# Revit family: Hager-Vector-IP65-vacío-ES-es
name_source: partatom
category: Electrical Equipment
units: mm (PartAtom-declared; Revit-internal decimal feet)

## family parameters
Cut with Voids When Loaded = No
Host = Face
Panel Configuration = Two Columns, Circuits Across
Part Type = Panelboard
Room Calculation Point = No
Round Connector Dimension = Use Diameter
Shared = No

## types (4) — shared parameters
EF000003 - Tipo de montaje = EV000384 - Montado superficial (escayola)
EF000007 - Color = EV000270 - Gris
EF000116 - Número RAL = 7035
EF000339 - Tipo de cubierta = EV004216 - Puerta
EF001062 - Versión de EMC = Yes
EF001088 - Posibilidad de extensión = Yes
EF001134 - Carril DIN = No
EF001596 - Material de la carcasa = EV000139 - Plástico
EF004462 - Tipo de cierre = EV000154 - Otros
EF005474 - Grado de protección (IP) = EV006421 - IP65
EF006244 - Tapa/puerta transparente = No
EF006306 - Con cierre = Yes
EF009212 - Versión de la cubierta = EV000116 - Cerrado
EF015776 - Borne de tierra = No
EF015777 - Borne neutro = No
EF015941 - Puerta de transmisión de señal = No
HG000002 - Con puerta o tapa = Yes
HG000003 - Gama = Vector
HG000005 - Grosor = 3 mm  [stored 0.00984252 ft]
HG000006 - Empotrado = No
HG000009 - Puerta batiente doble = No
HG000010 - Puertas asimétricas = No
HG000011 - Filas vacías desde abajo = No
HG000017 - Distancia entre polos = 18 mm  [stored 0.0590551 ft]
Manufacturer = Hager
Type Comments = Vector
zero-valued in all types: Default Elevation, EF000266 - Número de filas, EF000332 - Altura de la instalación, EF000846 - Anchura de instalación, EF002950 - Anchura de unidades de división, HG000001 - Número de columnas, HG000007 - Número de columnas vacías, HG000008 - Número de filas vacías

## per-type parameters (varying)
| type | EF000008 - Anchura | EF000040 - Altura | EF000049 - Profundidad | EF000118 - Con placa de montaje | EF000218 - Profundidad de instalación | EF001131 - Profundidad interna | HG000004 - Referencia del fabricante | Model |
| Montado superficial IP65 A250 A350 P160 0 unidad de división - VP20G | 250 mm  [stored 0.82021 ft] | 350 mm | 160 mm | Yes | 160 mm | 160 mm | VP20G | VP20G |
| Montado superficial IP65 A300 A500 P160 0 unidad de división - VP36G | 300 mm | 500 mm  [stored 1.64042 ft] | 160 mm | No | 160 mm | 160 mm | VP36G | VP36G |
| Montado superficial IP65 A400 A500 P210 0 unidad de división - VP54G | 400 mm  [stored 1.31234 ft] | 500 mm  [stored 1.64042 ft] | 210 mm  [stored 0.688976 ft] | No | 210 mm  [stored 0.688976 ft] | 210 mm  [stored 0.688976 ft] | VP54G | VP54G |
| Montado superficial IP65 A400 A650 P210 0 unidad de división - VP72G | 400 mm  [stored 1.31234 ft] | 650 mm  [stored 2.13255 ft] | 210 mm  [stored 0.688976 ft] | No | 210 mm  [stored 0.688976 ft] | 210 mm  [stored 0.688976 ft] | VP72G | VP72G |

note: [stored X ft] marks values corroborated as IEEE doubles in the binary element streams (Revit-internal decimal feet)

## geometry (parser evidence)
native form markers: Sweep x17
no freeform markers — native parametric forms only
